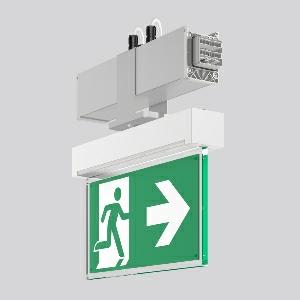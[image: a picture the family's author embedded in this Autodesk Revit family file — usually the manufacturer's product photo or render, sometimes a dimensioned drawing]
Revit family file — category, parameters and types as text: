
# Revit family: linedo_module_rz_9503rz_760_409_030_954f
name_source: partatom
category: Lighting Fixtures
units: mm (PartAtom-declared; Revit-internal decimal feet)

## family parameters
Cut with Voids When Loaded = No
Host = Face
Light Source = No
Part Type = Normal
Room Calculation Point = No
Round Connector Dimension = Use Diameter
Shared = No

## types (1)
- LINEDO Module RZ
    Apparent Load = 0 VA
    Default Elevation = 1800 mm
    Description = LINEDO, silver, on/off
Continuous line luminaire, L 336 B 62 H 343, CBS, AC-Control
    Height = 343 mm
    Lamp = 0 x
    Length = 336 mm
    Luminous efficacy = 0 lm/W
    Manufacturer = RZB
    ModVariant = No
    Model = 9503RZ.760.409.030
    Mounting Place = Ceiling
    Mounting Type = Surface mounted
    Number of Poles = 1
    OnlyDefault = Yes
    Power Factor = 1
    Product Name = LINEDO Module RZ
    Product group = Continuous line luminaire system Linedo IP 54
    ProductGroupID = 314
    Protection Class = Protection class I
    Protection Degree = IP 54
    RLX_Detail_Level = 1
    RLX_Emergency_Light_Flux = 0 lm
    RLX_Emergency_Type = 0
    RLX_Emergency_Type_DB = No
    RlxData = <blob elided: 37421 chars, md5=b33c5538>
    Standby Power = 0 W
    System Light Flux = 0 lm
    System Power = 0 W
    Type Comments = Product without accessories
    Type Image = 9503rz.760.434.030.jpg
    URL = http://relux.com
    VarID = ---
    Voltage = 0 V
    Weight = 0.00 kg
    Width = 62 mm  [stored 0.203412 ft]

note: [stored X ft] marks values corroborated as IEEE doubles in the binary element streams (Revit-internal decimal feet)

## geometry (parser evidence)
native form markers: Blend x4, Sweep x11
no freeform markers — native parametric forms only
